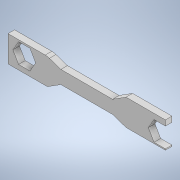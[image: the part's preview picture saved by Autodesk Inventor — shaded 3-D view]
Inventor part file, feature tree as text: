
AUTODESK INVENTOR PART (.ipt)
format: ipt  version: 2020.2 (Build 242310000, 310)  size: 131,072 bytes
history: native  units: in
note: dims shown in document units (in); Inventor stores cm internally (conversion verified against a paired STEP export)
features: extrude x1, sketch x1
ambient origin geometry x8: Origin, YZ Plane, XZ Plane, XY Plane, X Axis, Y Axis, Z Axis, Center Point
bodies: Solid1 (feature_tree)
feature tree (2):
  extrude  "Extrusion1"  Depth=0.75in
  sketch  "Sketch1"  dims[d1=1.0in d2=0.75in d3=0.1875in d4=0.75in d5=1.5in d6=1.5in d8=0.5in d9=0.5in d10=0.25in d11=0.0in]
